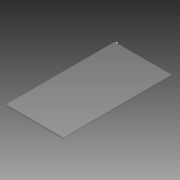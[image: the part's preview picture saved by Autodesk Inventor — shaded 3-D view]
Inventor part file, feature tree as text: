
AUTODESK INVENTOR PART (.ipt)
format: ipt  version: 2015 (Build 190159000, 159)  size: 93,696 bytes
history: native  units: in
note: dims shown in document units (in); Inventor stores cm internally (conversion verified against a paired STEP export)
features: sketch x3, extrude x2
ambient origin geometry x8: Origin, YZ Plane, XZ Plane, XY Plane, X Axis, Y Axis, Z Axis, Center Point
bodies: Solid1 (feature_tree)
feature tree (5):
  sketch  "Sketch1"  dims[d0=8.622in d1=0.2756in]
  extrude  "Extrusion1"  Depth=0.2756in
  extrude  "Extrusion2"  Depth=0.2524in
  sketch  "Sketch2"  dims[d2=16.6929in d3=0.0in d4=0.2524in]
  sketch  "Sketch3"  dims[d5=13.1688in d6=0.0in]
